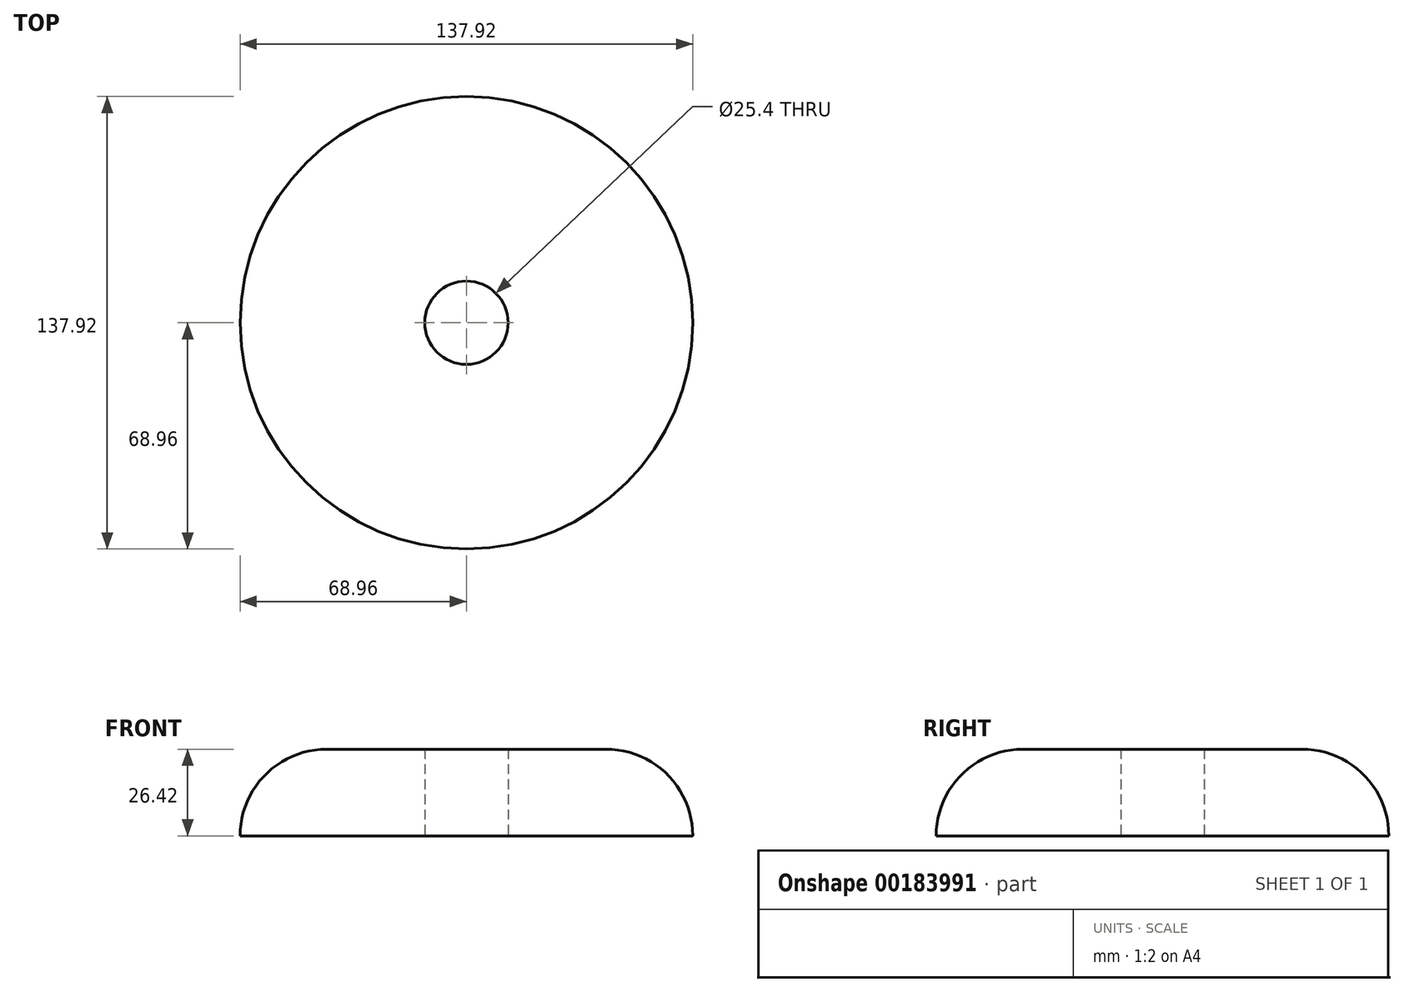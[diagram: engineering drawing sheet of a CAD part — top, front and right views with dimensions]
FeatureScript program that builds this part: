
annotation { "Feature Type Name" : "Feature", "Feature Type Description" : "" }
export const myFeature = defineFeature(function(context is Context, id is Id, definition is map)
    precondition{}
    {
        {
            var Q0;
            Q0=qCreatedBy(makeId("Top.planeOp"),FACE);
            var sketch = newSketch(context, id + "F0", { "sketchPlane" : qUnion([Q0])});
            skCircle(sketch, "E0", {"center": v(0, 0) * mm, "radius": 68.96 * mm});
            skSolve(sketch);
        }
        {
            var Q0;
            Q0=makeQuery(id+"F0.imprint","IMPRINT",FACE,{"disambiguationData":[TD([[makeQuery(id+"F0.imprint","IMPRINT",EDGE,{"derivedFrom":sQuery(id+"F0.wireOp",EDGE,"E0")}),1.0]])]});
            extrude(context, id + "F1", {"entities" : qUnion([Q0]), "depth" : 26.42 * mm});
        }
        {
            var Q0;
            Q0=makeQuery(id+"F1.opExtrude","CAP_FACE",FACE,{"disambiguationData":[OSD([sQuery(id+"F0.wireOp",EDGE,"E0")])],"isStart":false});
            fillet(context, id + "F2", {"entities" : qUnion([Q0]), "radius" : 26.37 * mm, "tangentPropagation" : true, "allowEdgeOverflow" : false});
        }
        {
            var Q0;
            Q0=makeQuery(id+"F1.opExtrude","CAP_FACE",FACE,{"disambiguationData":[OSD([sQuery(id+"F0.wireOp",EDGE,"E0")])],"isStart":true});
            var sketch = newSketch(context, id + "F3", { "sketchPlane" : qUnion([Q0])});
            skPoint(sketch, "E1", {"position": v(0, 0) * mm});
            skSolve(sketch);
        }
        {
            var Q0;
            Q0=sQuery(id+"F3.wireOp",VERTEX,"E1");
            var Q1;
            Q1=makeQuery(id+"F1.opExtrude","SWEPT_BODY",BODY,{"disambiguationData":[OSD([sQuery(id+"F0.wireOp",EDGE,"E0")])]});
            hole(context, id + "F4", {"style" : HoleStyle.SIMPLE, "endStyle" : HoleEndStyle.THROUGH, "holeDiameter" : 25.4 * mm, "locations" : qUnion([Q0]), "scope" : qUnion([Q1]), "isTappedThrough" : true});
        }
    });
